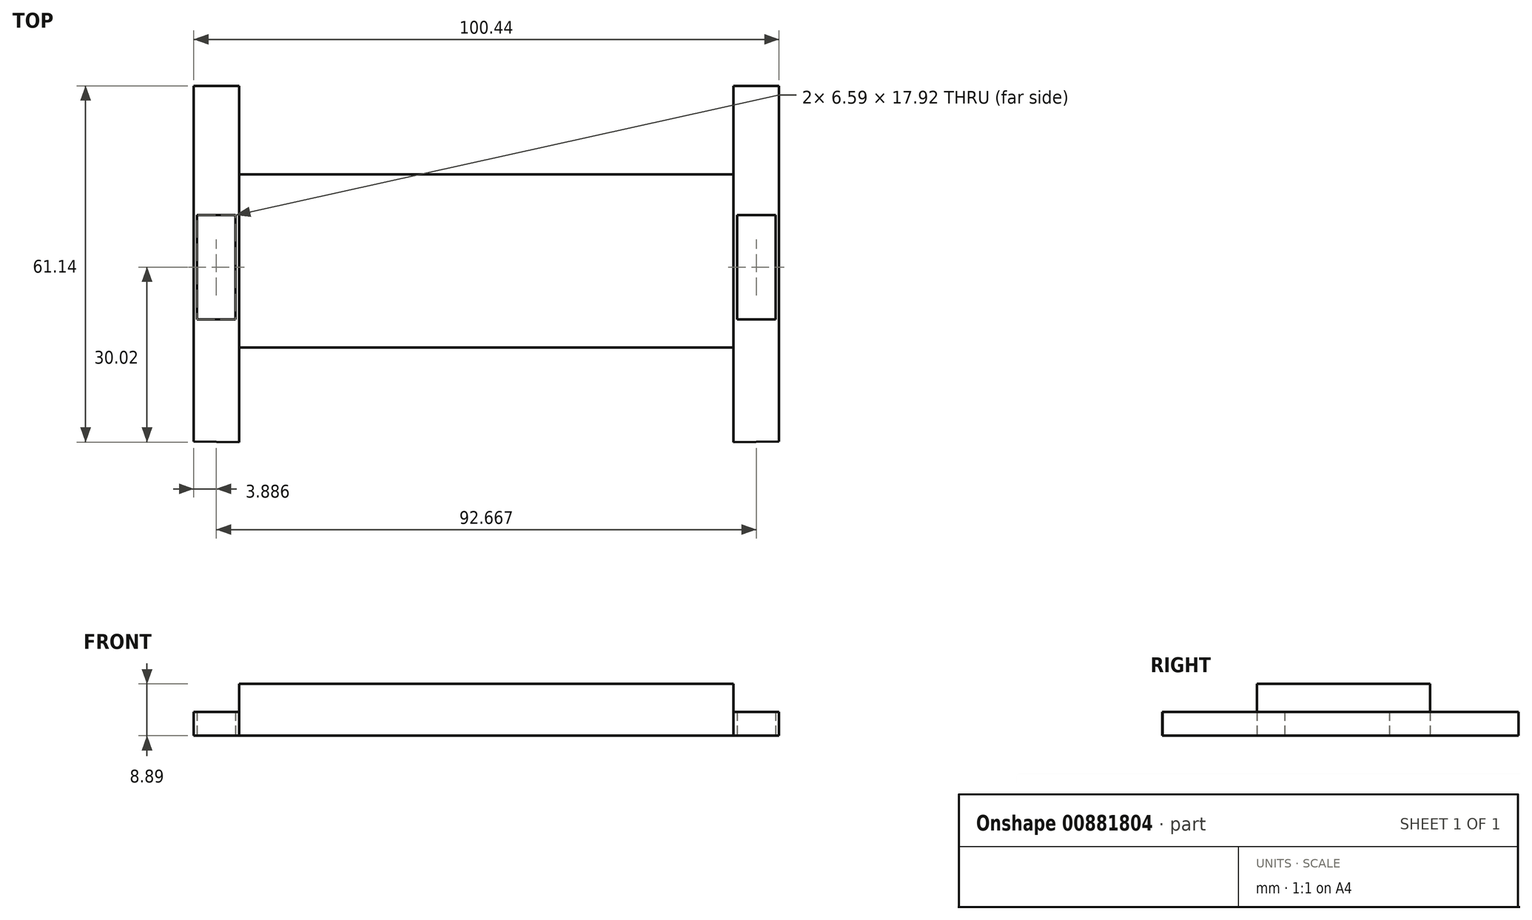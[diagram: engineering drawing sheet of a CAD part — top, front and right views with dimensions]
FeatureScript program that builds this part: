
annotation { "Feature Type Name" : "Feature", "Feature Type Description" : "" }
export const myFeature = defineFeature(function(context is Context, id is Id, definition is map)
    precondition{}
    {
        {
            var Q0;
            Q0=qCreatedBy(makeId("Top.planeOp"),FACE);
            var sketch = newSketch(context, id + "F0", { "sketchPlane" : qUnion([Q0])});
            skLineSegment(sketch, "E0", {"start": v(0, 15.97) * mm, "end": v(-42.41, 15.97) * mm});
            skLineSegment(sketch, "E1", {"start": v(-42.41, 15.97) * mm, "end": v(-42.41, -13.77) * mm});
            skLineSegment(sketch, "E2", {"start": v(-42.41, -13.77) * mm, "end": v(0, -13.77) * mm});
            skLineSegment(sketch, "E3", {"start": v(0, -13.77) * mm, "end": v(-42.41, -13.77) * mm});
            skLineSegment(sketch, "E4", {"start": v(-42.41, 31.12) * mm, "end": v(-42.41, 15.97) * mm});
            skLineSegment(sketch, "E5", {"start": v(-42.41, -13.77) * mm, "end": v(-42.41, -30.02) * mm});
            skLineSegment(sketch, "E6.MirrorCS", {"start": v(42.41, 31.12) * mm, "end": v(42.41, 15.97) * mm});
            skLineSegment(sketch, "E7.MirrorCS", {"start": v(42.41, -13.77) * mm, "end": v(42.41, -30.02) * mm});
            skLineSegment(sketch, "E8.MirrorCS", {"start": v(42.41, 15.97) * mm, "end": v(42.41, -13.77) * mm});
            skLineSegment(sketch, "E9.MirrorCS", {"start": v(0, 15.97) * mm, "end": v(42.41, 15.97) * mm});
            skLineSegment(sketch, "E10.MirrorCS", {"start": v(0, -13.77) * mm, "end": v(42.41, -13.77) * mm});
            skLineSegment(sketch, "E11", {"start": v(-42.41, 31.12) * mm, "end": v(-50.22, 31.12) * mm});
            skLineSegment(sketch, "E12", {"start": v(-50.22, 31.12) * mm, "end": v(-50.22, -29.92) * mm});
            skLineSegment(sketch, "E13", {"start": v(-50.22, -29.92) * mm, "end": v(-42.41, -30.02) * mm});
            skLineSegment(sketch, "E14.MirrorCS", {"start": v(42.41, 31.12) * mm, "end": v(50.22, 31.12) * mm});
            skLineSegment(sketch, "E15.MirrorCS", {"start": v(50.22, 31.12) * mm, "end": v(50.22, -29.92) * mm});
            skLineSegment(sketch, "E16.MirrorCS", {"start": v(50.22, -29.92) * mm, "end": v(42.41, -30.02) * mm});
            skSolve(sketch);
        }
        {
            var Q0;
            Q0 = qSketchRegion(id + "F0", true);
            extrude(context, id + "F1", {"entities" : qUnion([Q0]), "depth" : 4.06 * mm, "offsetDistance" : 25.4 * mm});
        }
        {
            var Q0;
            Q0=makeQuery(id+"F1.opExtrude","CAP_FACE",FACE,{"disambiguationData":[OSD([sQuery(id+"F0.wireOp",EDGE,"E0"),sQuery(id+"F0.wireOp",EDGE,"E3"),sQuery(id+"F0.wireOp",EDGE,"E4"),sQuery(id+"F0.wireOp",EDGE,"E5"),sQuery(id+"F0.wireOp",EDGE,"E6.MirrorCS"),sQuery(id+"F0.wireOp",EDGE,"E7.MirrorCS"),sQuery(id+"F0.wireOp",EDGE,"E9.MirrorCS"),sQuery(id+"F0.wireOp",EDGE,"E10.MirrorCS"),sQuery(id+"F0.wireOp",EDGE,"E11"),sQuery(id+"F0.wireOp",EDGE,"E12"),sQuery(id+"F0.wireOp",EDGE,"E13"),sQuery(id+"F0.wireOp",EDGE,"E14.MirrorCS"),sQuery(id+"F0.wireOp",EDGE,"E15.MirrorCS"),sQuery(id+"F0.wireOp",EDGE,"E16.MirrorCS")])],"isStart":false});
            var sketch = newSketch(context, id + "F2", { "sketchPlane" : qUnion([Q0])});
            skLineSegment(sketch, "E17", {"start": v(-42.41, 15.97) * mm, "end": v(-42.41, -13.77) * mm});
            skLineSegment(sketch, "E18", {"start": v(42.41, 15.97) * mm, "end": v(42.41, -13.77) * mm});
            skLineSegment(sketch, "E19", {"start": v(-42.41, -13.77) * mm, "end": v(42.41, -13.77) * mm});
            skLineSegment(sketch, "E20", {"start": v(-42.41, 15.97) * mm, "end": v(42.41, 15.97) * mm});
            skLineSegment(sketch, "E21", {"start": v(-42.41, 15.97) * mm, "end": v(-50.22, 15.97) * mm});
            skLineSegment(sketch, "E22", {"start": v(-42.41, -13.77) * mm, "end": v(-50.22, -13.77) * mm});
            skLineSegment(sketch, "E23", {"start": v(42.41, -13.77) * mm, "end": v(50.22, -13.77) * mm});
            skLineSegment(sketch, "E24", {"start": v(42.41, 15.97) * mm, "end": v(50.22, 15.97) * mm});
            skSolve(sketch);
        }
        {
            var Q0;
            Q0 = qSketchRegion(id + "F2", true);
            extrude(context, id + "F3", {"entities" : qUnion([Q0]), "operationType" : NewBodyOperationType.ADD, "depth" : 4.83 * mm, "offsetDistance" : 25.4 * mm});
        }
        {
            var Q0;
            Q0=qCreatedBy(makeId("Top.planeOp"),FACE);
            var sketch = newSketch(context, id + "F4", { "sketchPlane" : qUnion([Q0])});
            skLineSegment(sketch, "E25.bottom", {"start": v(43.04, 8.96) * mm, "end": v(49.63, 8.96) * mm});
            skLineSegment(sketch, "E25.top", {"start": v(43.04, -8.96) * mm, "end": v(49.63, -8.96) * mm});
            skLineSegment(sketch, "E25.left", {"start": v(49.63, 8.96) * mm, "end": v(49.63, -8.96) * mm});
            skLineSegment(sketch, "E25.right", {"start": v(43.04, 8.96) * mm, "end": v(43.04, -8.96) * mm});
            skPoint(sketch, "E25.middle", {"position": v(46.33, 0) * mm});
            skLineSegment(sketch, "E26.MirrorCS", {"start": v(-43.04, 8.96) * mm, "end": v(-49.63, 8.96) * mm});
            skLineSegment(sketch, "E27.MirrorCS", {"start": v(-43.04, 8.96) * mm, "end": v(-43.04, -8.96) * mm});
            skLineSegment(sketch, "E28.MirrorCS", {"start": v(-49.63, 8.96) * mm, "end": v(-49.63, -8.96) * mm});
            skLineSegment(sketch, "E29.MirrorCS", {"start": v(-43.04, -8.96) * mm, "end": v(-49.63, -8.96) * mm});
            skSolve(sketch);
        }
        {
            var Q0;
            Q0 = qSketchRegion(id + "F4", true);
            extrude(context, id + "F5", {"entities" : qUnion([Q0]), "operationType" : NewBodyOperationType.REMOVE, "depth" : 27.94 * mm, "offsetDistance" : 25.4 * mm});
        }
    });
